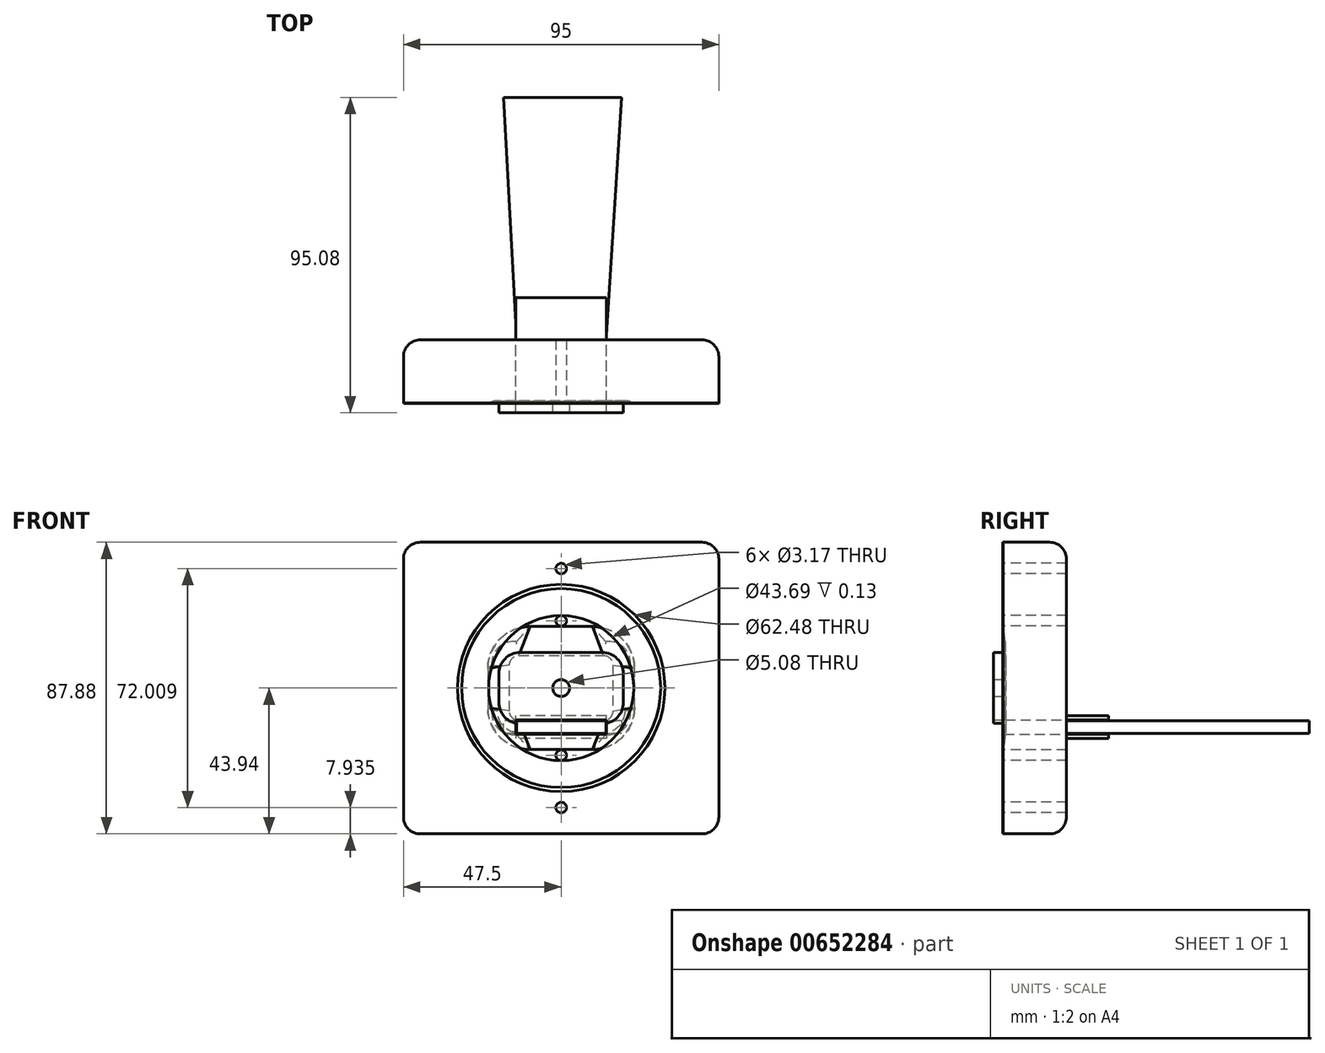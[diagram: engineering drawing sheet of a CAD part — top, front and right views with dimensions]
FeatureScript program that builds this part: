
annotation { "Feature Type Name" : "Feature", "Feature Type Description" : "" }
export const myFeature = defineFeature(function(context is Context, id is Id, definition is map)
    precondition{}
    {
        {
            assignVariable(context, id + "F0", {"name" : "RingLightT", "anyValue" : .13});
        }
        {
            assignVariable(context, id + "F1", {"name" : "CamDepth", "anyValue" : .688});
        }
        {
            var Q0;
            Q0=qCreatedBy(makeId("Front.planeOp"),FACE);
            var sketch = newSketch(context, id + "F2", { "sketchPlane" : qUnion([Q0])});
            skCircle(sketch, "E0", {"center": v(0, 0) * mm, "radius": 21.84 * mm});
            skCircle(sketch, "E1", {"center": v(0, 0) * mm, "radius": 29.97 * mm});
            skSolve(sketch);
        }
        {
            var Q0;
            Q0=qSketchRegion(id+"F2",true);
            extrude(context, id + "F3", {"entities" : qUnion([Q0]), "depth" : (getVariable(context, 'RingLightT')) * mm, "offsetDistance" : 25.4 * mm});
        }
        {
            var Q0;
            Q0=qCreatedBy(makeId("Front.planeOp"),FACE);
            var sketch = newSketch(context, id + "F4", { "sketchPlane" : qUnion([Q0])});
            skLineSegment(sketch, "E2.bottom", {"start": v(12.38, 10.73) * mm, "end": v(-12.38, 10.73) * mm});
            skLineSegment(sketch, "E2.top", {"start": v(12.38, -10.73) * mm, "end": v(-12.38, -10.73) * mm});
            skLineSegment(sketch, "E2.left", {"start": v(18.73, 4.38) * mm, "end": v(18.73, -4.38) * mm});
            skLineSegment(sketch, "E2.right", {"start": v(-18.73, 4.38) * mm, "end": v(-18.73, -4.38) * mm});
            skPoint(sketch, "E2.middle", {"position": v(0, 0) * mm});
            skPoint(sketch, "E3.visualSharp", {"position": v(-18.73, 10.73) * mm});
            skArc(sketch, "E3.filletArc", {"start": v(-12.38, 10.73) * mm, "mid": v(-16.87, 8.87) * mm, "end": v(-18.73, 4.38) * mm});
            skPoint(sketch, "E4.visualSharp", {"position": v(18.73, 10.73) * mm});
            skArc(sketch, "E4.filletArc", {"start": v(18.73, 4.38) * mm, "mid": v(16.87, 8.87) * mm, "end": v(12.38, 10.73) * mm});
            skPoint(sketch, "E5.visualSharp", {"position": v(18.73, -10.73) * mm});
            skArc(sketch, "E5.filletArc", {"start": v(12.38, -10.73) * mm, "mid": v(16.87, -8.87) * mm, "end": v(18.73, -4.38) * mm});
            skPoint(sketch, "E6.visualSharp", {"position": v(-18.73, -10.73) * mm});
            skArc(sketch, "E6.filletArc", {"start": v(-18.73, -4.38) * mm, "mid": v(-16.87, -8.87) * mm, "end": v(-12.38, -10.73) * mm});
            skCircle(sketch, "E7", {"center": v(0, 0) * mm, "radius": 2.54 * mm});
            skSolve(sketch);
        }
        {
            var Q0;
            Q0=qSketchRegion(id+"F4",true);
            extrude(context, id + "F5", {"entities" : qUnion([Q0]), "depth" : 2.95 * mm, "offsetDistance" : 25.4 * mm});
        }
        {
            var Q0;
            Q0=qCreatedBy(makeId("Front.planeOp"),FACE);
            cPlane(context, id + "F6", {"entities" : qUnion([Q0]), "cplaneType" : CPlaneType.OFFSET, "offset" : (getVariable(context, 'CamDepth')) * mm, "oppositeDirection" : true, "width" : 152.4 * mm, "height" : 152.4 * mm});
        }
        {
            var Q0;
            Q0=qCreatedBy(id+"F6.planeOp",FACE);
            var sketch = newSketch(context, id + "F7", { "sketchPlane" : qUnion([Q0])});
            skLineSegment(sketch, "E8.bottom", {"start": v(13.7, 13.68) * mm, "end": v(-13.7, 13.68) * mm});
            skLineSegment(sketch, "E8.top", {"start": v(13.7, -13.68) * mm, "end": v(-13.7, -13.68) * mm});
            skLineSegment(sketch, "E8.left", {"start": v(20.04, 7.33) * mm, "end": v(20.04, -7.33) * mm});
            skLineSegment(sketch, "E8.right", {"start": v(-20.04, 7.33) * mm, "end": v(-20.04, -7.33) * mm});
            skPoint(sketch, "E8.middle", {"position": v(0, 0) * mm});
            skPoint(sketch, "E9.visualSharp", {"position": v(-20.04, 13.68) * mm});
            skArc(sketch, "E9.filletArc", {"start": v(-13.7, 13.68) * mm, "mid": v(-18.18, 11.82) * mm, "end": v(-20.04, 7.33) * mm});
            skPoint(sketch, "E10.visualSharp", {"position": v(20.04, 13.68) * mm});
            skArc(sketch, "E10.filletArc", {"start": v(20.04, 7.33) * mm, "mid": v(18.18, 11.82) * mm, "end": v(13.7, 13.68) * mm});
            skPoint(sketch, "E11.visualSharp", {"position": v(20.04, -13.68) * mm});
            skArc(sketch, "E11.filletArc", {"start": v(13.7, -13.68) * mm, "mid": v(18.18, -11.82) * mm, "end": v(20.04, -7.33) * mm});
            skPoint(sketch, "E12.visualSharp", {"position": v(-20.04, -13.68) * mm});
            skArc(sketch, "E12.filletArc", {"start": v(-20.04, -7.33) * mm, "mid": v(-18.18, -11.82) * mm, "end": v(-13.7, -13.68) * mm});
            skSolve(sketch);
        }
        {
            var Q0;
            Q0=qCreatedBy(makeId("Front.planeOp"),FACE);
            var sketch = newSketch(context, id + "F8", { "sketchPlane" : qUnion([Q0])});
            skLineSegment(sketch, "E13.bottom", {"start": v(9.4, 18.54) * mm, "end": v(-9.4, 18.54) * mm});
            skLineSegment(sketch, "E13.top", {"start": v(9.4, -18.54) * mm, "end": v(-9.4, -18.54) * mm});
            skLineSegment(sketch, "E13.left", {"start": v(22.1, 5.84) * mm, "end": v(22.1, -5.84) * mm});
            skLineSegment(sketch, "E13.right", {"start": v(-22.1, 5.84) * mm, "end": v(-22.1, -5.84) * mm});
            skPoint(sketch, "E13.middle", {"position": v(0, 0) * mm});
            skPoint(sketch, "E14.visualSharp", {"position": v(-22.1, 18.54) * mm});
            skArc(sketch, "E14.filletArc", {"start": v(-9.4, 18.54) * mm, "mid": v(-18.38, 14.82) * mm, "end": v(-22.1, 5.84) * mm});
            skPoint(sketch, "E15.visualSharp", {"position": v(22.1, 18.54) * mm});
            skArc(sketch, "E15.filletArc", {"start": v(22.1, 5.84) * mm, "mid": v(18.38, 14.82) * mm, "end": v(9.4, 18.54) * mm});
            skPoint(sketch, "E16.visualSharp", {"position": v(22.1, -18.54) * mm});
            skArc(sketch, "E16.filletArc", {"start": v(9.4, -18.54) * mm, "mid": v(18.38, -14.82) * mm, "end": v(22.1, -5.84) * mm});
            skPoint(sketch, "E17.visualSharp", {"position": v(-22.1, -18.54) * mm});
            skArc(sketch, "E17.filletArc", {"start": v(-22.1, -5.84) * mm, "mid": v(-18.38, -14.82) * mm, "end": v(-9.4, -18.54) * mm});
            skSolve(sketch);
        }
        {
            var Q1;
            Q1=makeQuery(id+"F7.imprint","IMPRINT",FACE,{"disambiguationData":[TD([[makeQuery(id+"F7.imprint","IMPRINT",EDGE,{"derivedFrom":sQuery(id+"F7.wireOp",EDGE,"E8.bottom")}),1.0]])]});
            var Q2;
            Q2=makeQuery(id+"F8.imprint","IMPRINT",FACE,{"disambiguationData":[TD([[makeQuery(id+"F8.imprint","IMPRINT",EDGE,{"derivedFrom":sQuery(id+"F8.wireOp",EDGE,"E13.bottom")}),1.0]])]});
            loft(context, id + "F9", {"operationType" : NewBodyOperationType.ADD, "sheetProfilesArray" : [{ "sheetProfileEntities" : qUnion([Q1]) }, { "sheetProfileEntities" : qUnion([Q2]) }]});
        }
        {
            var Q0;
            Q0=makeQuery(id+"F9.opLoft","CAP_FACE",FACE,{"disambiguationData":[OSD([makeQuery(id+"F7.imprint","IMPRINT",FACE,{"disambiguationData":[TD([[makeQuery(id+"F7.imprint","IMPRINT",EDGE,{"derivedFrom":sQuery(id+"F7.wireOp",EDGE,"E8.bottom")}),1.0]])]})])],"isStart":true});
            var sketch = newSketch(context, id + "F10", { "sketchPlane" : qUnion([Q0])});
            skLineSegment(sketch, "E18.bottom", {"start": v(-12.38, -13.68) * mm, "end": v(12.38, -13.68) * mm});
            skLineSegment(sketch, "E18.top", {"start": v(-12.38, -9.84) * mm, "end": v(12.38, -9.84) * mm});
            skLineSegment(sketch, "E18.left", {"start": v(-12.38, -13.68) * mm, "end": v(-12.38, -9.84) * mm});
            skLineSegment(sketch, "E18.right", {"start": v(12.38, -13.68) * mm, "end": v(12.38, -9.84) * mm});
            skPoint(sketch, "E19", {"position": v(0, -13.68) * mm});
            skSolve(sketch);
        }
        {
            var Q0;
            Q0=makeQuery(id+"F9.opLoft","CAP_FACE",FACE,{"disambiguationData":[OSD([makeQuery(id+"F7.imprint","IMPRINT",FACE,{"disambiguationData":[TD([[makeQuery(id+"F7.imprint","IMPRINT",EDGE,{"derivedFrom":sQuery(id+"F7.wireOp",EDGE,"E8.bottom")}),1.0]])]})])],"isStart":true});
            cPlane(context, id + "F11", {"entities" : qUnion([Q0]), "cplaneType" : CPlaneType.OFFSET, "offset" : 91.44 * mm, "width" : 152.4 * mm, "height" : 152.4 * mm});
        }
        {
            var Q0;
            Q0=qCreatedBy(id+"F11.planeOp",FACE);
            var sketch = newSketch(context, id + "F12", { "sketchPlane" : qUnion([Q0])});
            skLineSegment(sketch, "E20.0", {"start": v(-12.38, -9.84) * mm, "end": v(12.38, -9.84) * mm, "construction": true});
            skLineSegment(sketch, "E21.0", {"start": v(12.38, -13.68) * mm, "end": v(12.38, -9.84) * mm, "construction": true});
            skLineSegment(sketch, "E22.0", {"start": v(-12.38, -13.68) * mm, "end": v(-12.38, -9.84) * mm, "construction": true});
            skLineSegment(sketch, "E23.0", {"start": v(-12.38, -13.68) * mm, "end": v(12.38, -13.68) * mm, "construction": true});
            skLineSegment(sketch, "E24", {"start": v(-18.23, -9.84) * mm, "end": v(17.33, -9.84) * mm});
            skLineSegment(sketch, "E25", {"start": v(-18.23, -9.84) * mm, "end": v(-18.23, -13.68) * mm});
            skLineSegment(sketch, "E26", {"start": v(-18.23, -13.68) * mm, "end": v(17.33, -13.68) * mm});
            skLineSegment(sketch, "E27", {"start": v(17.33, -13.68) * mm, "end": v(17.33, -9.84) * mm});
            skSolve(sketch);
        }
        {
            var Q0;
            Q0=qSketchRegion(id+"F10",true);
            var Q1;
            Q1=qSketchRegion(id+"F12",true);
            loft(context, id + "F13", {"sheetProfilesArray" : [{ "sheetProfileEntities" : qUnion([Q0]) }, { "sheetProfileEntities" : qUnion([Q1]) }]});
        }
        {
            var Q0;
            Q0=makeQuery(id+"F9.opLoft","MID_CAP_EDGE",EDGE,{"disambiguationData":[OSD([sQuery(id+"F7.wireOp",EDGE,"E8.bottom"),sQuery(id+"F7.wireOp",EDGE,"E9.filletArc"),sQuery(id+"F7.wireOp",EDGE,"E10.filletArc")])],"capPos":0.0});
            fillet(context, id + "F14", {"entities" : qUnion([Q0]), "radius" : 5.08 * mm, "tangentPropagation" : true, "allowEdgeOverflow" : false});
        }
        {
            var Q0;
            {var subQ2=sQuery(id+"F8.wireOp",EDGE,"E13.bottom");Q0=makeQuery(id+"F9.boolean.opBoolean","SPLIT",FACE,{"disambiguationData":[TD([makeQuery(id+"F5.opExtrude","SWEPT_FACE",FACE,{"disambiguationData":[OSD([sQuery(id+"F4.wireOp",EDGE,"E2.bottom")])]})])],"derivedFrom":makeQuery(id+"F9.opLoft","CAP_FACE",FACE,{"disambiguationData":[OSD([makeQuery(id+"F8.imprint","IMPRINT",FACE,{"disambiguationData":[TD([[makeQuery(id+"F8.imprint","IMPRINT",EDGE,{"derivedFrom":subQ2}),1.0]])]})])],"isStart":true})});}
            var sketch = newSketch(context, id + "F15", { "sketchPlane" : qUnion([Q0])});
            skLineSegment(sketch, "E28.bottom", {"start": v(47.5, 43.94) * mm, "end": v(-47.5, 43.94) * mm});
            skLineSegment(sketch, "E28.top", {"start": v(47.5, -43.94) * mm, "end": v(-47.5, -43.94) * mm});
            skLineSegment(sketch, "E28.left", {"start": v(47.5, 43.94) * mm, "end": v(47.5, -43.94) * mm});
            skLineSegment(sketch, "E28.right", {"start": v(-47.5, 43.94) * mm, "end": v(-47.5, -43.94) * mm});
            skPoint(sketch, "E28.middle", {"position": v(0, 0) * mm});
            skCircle(sketch, "E29", {"center": v(0, 0) * mm, "radius": 31.24 * mm});
            skSolve(sketch);
        }
        {
            var Q0;
            Q0=qSketchRegion(id+"F15",true);
            extrude(context, id + "F16", {"entities" : qUnion([Q0]), "depth" : (getVariable(context, 'RingLightT')) * mm, "offsetDistance" : 25.4 * mm});
        }
        {
            var Q0;
            Q0=makeQuery(id+"F16.opExtrude","CAP_FACE",FACE,{"disambiguationData":[OSD([sQuery(id+"F15.wireOp",EDGE,"E28.bottom"),sQuery(id+"F15.wireOp",EDGE,"E28.top"),sQuery(id+"F15.wireOp",EDGE,"E28.left"),sQuery(id+"F15.wireOp",EDGE,"E28.right"),sQuery(id+"F15.wireOp",EDGE,"E29")])],"isStart":true});
            var sketch = newSketch(context, id + "F17", { "sketchPlane" : qUnion([Q0])});
            skLineSegment(sketch, "E30.bottom", {"start": v(47.5, 43.94) * mm, "end": v(-47.5, 43.94) * mm});
            skLineSegment(sketch, "E30.top", {"start": v(47.5, -43.94) * mm, "end": v(-47.5, -43.94) * mm});
            skLineSegment(sketch, "E30.left", {"start": v(47.5, 43.94) * mm, "end": v(47.5, -43.94) * mm});
            skLineSegment(sketch, "E30.right", {"start": v(-47.5, 43.94) * mm, "end": v(-47.5, -43.94) * mm});
            skPoint(sketch, "E30.middle", {"position": v(0, 0) * mm});
            skSolve(sketch);
        }
        {
            var Q0;
            Q0=qSketchRegion(id+"F17",true);
            extrude(context, id + "F18", {"entities" : qUnion([Q0]), "depth" : 19.05 * mm, "offsetDistance" : 25.4 * mm});
        }
        {
            var Q0;
            Q0=qCreatedBy(makeId("Front.planeOp"),FACE);
            var sketch = newSketch(context, id + "F19", { "sketchPlane" : qUnion([Q0])});
            skFitSpline(sketch, "E31.0", {"points": [v(-22.1, 5.84) * mm, v(-22.1, 6.26) * mm, v(-22.06, 7.09) * mm, v(-21.87, 8.32) * mm, v(-21.57, 9.53) * mm, v(-21.15, 10.71) * mm, v(-20.62, 11.84) * mm, v(-19.97, 12.9) * mm, v(-19.23, 13.91) * mm, v(-18.4, 14.84) * mm, v(-17.47, 15.67) * mm, v(-16.46, 16.42) * mm, v(-15.4, 17.06) * mm, v(-14.27, 17.6) * mm, v(-13.1, 18.01) * mm, v(-11.88, 18.32) * mm, v(-10.64, 18.5) * mm, v(-9.82, 18.54) * mm, v(-9.4, 18.54) * mm]});
            skLineSegment(sketch, "E32.0", {"start": v(9.4, 18.54) * mm, "end": v(-9.4, 18.54) * mm});
            skFitSpline(sketch, "E33.0", {"points": [v(9.4, 18.54) * mm, v(9.81, 18.54) * mm, v(10.64, 18.5) * mm, v(11.88, 18.32) * mm, v(13.1, 18.02) * mm, v(14.27, 17.6) * mm, v(15.4, 17.06) * mm, v(16.47, 16.42) * mm, v(17.47, 15.68) * mm, v(18.4, 14.84) * mm, v(19.23, 13.91) * mm, v(19.97, 12.9) * mm, v(20.62, 11.84) * mm, v(21.15, 10.7) * mm, v(21.57, 9.54) * mm, v(21.87, 8.32) * mm, v(22.06, 7.09) * mm, v(22.1, 6.26) * mm, v(22.1, 5.84) * mm]});
            skLineSegment(sketch, "E34.0", {"start": v(-22.1, 5.84) * mm, "end": v(-22.1, -5.84) * mm});
            skFitSpline(sketch, "E35.0", {"points": [v(22.1, -5.84) * mm, v(22.1, -6.26) * mm, v(22.06, -7.09) * mm, v(21.87, -8.32) * mm, v(21.57, -9.53) * mm, v(21.15, -10.71) * mm, v(20.62, -11.84) * mm, v(19.97, -12.9) * mm, v(19.23, -13.91) * mm, v(18.4, -14.84) * mm, v(17.47, -15.67) * mm, v(16.46, -16.42) * mm, v(15.4, -17.06) * mm, v(14.27, -17.6) * mm, v(13.1, -18.01) * mm, v(11.88, -18.32) * mm, v(10.64, -18.5) * mm, v(9.82, -18.54) * mm, v(9.4, -18.54) * mm]});
            skLineSegment(sketch, "E36.0", {"start": v(-9.4, -18.54) * mm, "end": v(9.4, -18.54) * mm});
            skFitSpline(sketch, "E37.0", {"points": [v(-9.4, -18.54) * mm, v(-9.81, -18.54) * mm, v(-10.64, -18.5) * mm, v(-11.88, -18.32) * mm, v(-13.1, -18.02) * mm, v(-14.27, -17.6) * mm, v(-15.4, -17.06) * mm, v(-16.47, -16.42) * mm, v(-17.47, -15.68) * mm, v(-18.4, -14.84) * mm, v(-19.23, -13.91) * mm, v(-19.97, -12.9) * mm, v(-20.62, -11.84) * mm, v(-21.15, -10.7) * mm, v(-21.57, -9.54) * mm, v(-21.87, -8.32) * mm, v(-22.06, -7.09) * mm, v(-22.1, -6.26) * mm, v(-22.1, -5.84) * mm]});
            skLineSegment(sketch, "E38.0", {"start": v(22.1, -5.84) * mm, "end": v(22.1, 5.84) * mm});
            skSolve(sketch);
        }
        {
            var Q0;
            Q0=makeQuery(id+"F9.opLoft","CAP_FACE",FACE,{"disambiguationData":[OSD([makeQuery(id+"F7.imprint","IMPRINT",FACE,{"disambiguationData":[TD([[makeQuery(id+"F7.imprint","IMPRINT",EDGE,{"derivedFrom":sQuery(id+"F7.wireOp",EDGE,"E8.bottom")}),1.0]])]})])],"isStart":true});
            var sketch = newSketch(context, id + "F20", { "sketchPlane" : qUnion([Q0])});
            skFitSpline(sketch, "E39.0", {"points": [v(-12.78, 9.82) * mm, v(-12.96, 9.82) * mm, v(-13.32, 9.77) * mm, v(-13.85, 9.6) * mm, v(-14.25, 9.37) * mm, v(-14.54, 9.14) * mm, v(-14.74, 8.95) * mm, v(-14.91, 8.74) * mm, v(-15.07, 8.52) * mm, v(-15.2, 8.27) * mm, v(-15.35, 7.94) * mm, v(-15.48, 7.5) * mm, v(-15.52, 7.13) * mm, v(-15.52, 6.95) * mm]});
            skLineSegment(sketch, "E40.0", {"start": v(12.78, 9.82) * mm, "end": v(-12.78, 9.82) * mm});
            skFitSpline(sketch, "E41.0", {"points": [v(15.52, 6.95) * mm, v(15.52, 7.13) * mm, v(15.49, 7.5) * mm, v(15.33, 8.03) * mm, v(15.09, 8.52) * mm, v(14.75, 8.96) * mm, v(14.34, 9.32) * mm, v(13.85, 9.6) * mm, v(13.33, 9.77) * mm, v(12.96, 9.82) * mm, v(12.78, 9.82) * mm]});
            skLineSegment(sketch, "E42.0", {"start": v(15.52, -6.95) * mm, "end": v(15.52, 6.95) * mm});
            skFitSpline(sketch, "E43.0", {"points": [v(12.78, -9.82) * mm, v(12.96, -9.82) * mm, v(13.32, -9.77) * mm, v(13.85, -9.6) * mm, v(14.25, -9.37) * mm, v(14.54, -9.14) * mm, v(14.74, -8.95) * mm, v(14.91, -8.74) * mm, v(15.07, -8.52) * mm, v(15.2, -8.27) * mm, v(15.35, -7.94) * mm, v(15.48, -7.5) * mm, v(15.52, -7.13) * mm, v(15.52, -6.95) * mm]});
            skLineSegment(sketch, "E44.0", {"start": v(-12.78, -9.82) * mm, "end": v(12.78, -9.82) * mm});
            skFitSpline(sketch, "E45.0", {"points": [v(-15.52, -6.95) * mm, v(-15.52, -7.13) * mm, v(-15.49, -7.5) * mm, v(-15.33, -8.03) * mm, v(-15.09, -8.52) * mm, v(-14.75, -8.96) * mm, v(-14.34, -9.32) * mm, v(-13.85, -9.6) * mm, v(-13.33, -9.77) * mm, v(-12.96, -9.82) * mm, v(-12.78, -9.82) * mm]});
            skLineSegment(sketch, "E46.0", {"start": v(-15.52, 6.95) * mm, "end": v(-15.52, -6.95) * mm});
            skSolve(sketch);
        }
        {
            var Q1;
            Q1=qSketchRegion(id+"F20",true);
            var Q2;
            Q2=qSketchRegion(id+"F19",true);
            loft(context, id + "F21", {"operationType" : NewBodyOperationType.REMOVE, "sheetProfilesArray" : [{ "sheetProfileEntities" : qUnion([Q1]) }, { "sheetProfileEntities" : qUnion([Q2]) }]});
        }
        {
            var Q0;
            Q0=makeQuery(id+"F18.opExtrude","CAP_FACE",FACE,{"disambiguationData":[OSD([sQuery(id+"F17.wireOp",EDGE,"E30.bottom"),sQuery(id+"F17.wireOp",EDGE,"E30.top"),sQuery(id+"F17.wireOp",EDGE,"E30.left"),sQuery(id+"F17.wireOp",EDGE,"E30.right")])],"isStart":false});
            var sketch = newSketch(context, id + "F22", { "sketchPlane" : qUnion([Q0])});
            skLineSegment(sketch, "E47.0", {"start": v(-13.65, -9.59) * mm, "end": v(13.65, -9.59) * mm});
            skLineSegment(sketch, "E47.1", {"start": v(-13.65, -13.93) * mm, "end": v(-13.65, -9.59) * mm});
            skLineSegment(sketch, "E47.2", {"start": v(13.65, -13.93) * mm, "end": v(-13.65, -13.93) * mm});
            skLineSegment(sketch, "E47.3", {"start": v(13.65, -13.93) * mm, "end": v(13.65, -9.59) * mm});
            skLineSegment(sketch, "E48.0", {"start": v(-12.38, -9.84) * mm, "end": v(12.38, -9.84) * mm, "construction": true});
            skLineSegment(sketch, "E49.0", {"start": v(-12.38, -13.68) * mm, "end": v(-12.38, -9.84) * mm, "construction": true});
            skLineSegment(sketch, "E50.0", {"start": v(-12.38, -13.68) * mm, "end": v(12.38, -13.68) * mm, "construction": true});
            skPoint(sketch, "E51.0", {"position": v(12.38, -11.76) * mm});
            skLineSegment(sketch, "E52.0", {"start": v(12.38, -13.68) * mm, "end": v(12.38, -9.84) * mm, "construction": true});
            skSolve(sketch);
        }
        {
            var Q0;
            Q0=qSketchRegion(id+"F22",true);
            extrude(context, id + "F23", {"entities" : qUnion([Q0]), "operationType" : NewBodyOperationType.REMOVE, "oppositeDirection" : true, "depth" : 25.4 * mm, "offsetDistance" : 25.4 * mm});
        }
        {
            var Q0;
            Q0=makeQuery(id+"F18.opExtrude","CAP_FACE",FACE,{"disambiguationData":[OSD([sQuery(id+"F17.wireOp",EDGE,"E30.bottom"),sQuery(id+"F17.wireOp",EDGE,"E30.top"),sQuery(id+"F17.wireOp",EDGE,"E30.left"),sQuery(id+"F17.wireOp",EDGE,"E30.right")])],"isStart":true});
            var sketch = newSketch(context, id + "F24", { "sketchPlane" : qUnion([Q0])});
            skCircle(sketch, "E53", {"center": v(0, 20.26) * mm, "radius": 1.59 * mm});
            skCircle(sketch, "E54", {"center": v(0, -20.26) * mm, "radius": 1.59 * mm});
            skSolve(sketch);
        }
        {
            var Q0;
            Q0=qSketchRegion(id+"F24",true);
            var Q1;
            Q1=makeQuery(id+"F18.opExtrude","CAP_FACE",FACE,{"disambiguationData":[OSD([sQuery(id+"F17.wireOp",EDGE,"E30.bottom"),sQuery(id+"F17.wireOp",EDGE,"E30.top"),sQuery(id+"F17.wireOp",EDGE,"E30.left"),sQuery(id+"F17.wireOp",EDGE,"E30.right")])],"isStart":false});
            extrude(context, id + "F25", {"entities" : qUnion([Q0]), "operationType" : NewBodyOperationType.REMOVE, "endBound" : BoundingType.UP_TO_SURFACE, "oppositeDirection" : true, "depth" : 25.4 * mm, "endBoundEntityFace" : qUnion([Q1]), "offsetDistance" : 25.4 * mm});
        }
        {
            var Q0;
            Q0=makeQuery(id+"F16.opExtrude","CAP_FACE",FACE,{"disambiguationData":[OSD([sQuery(id+"F15.wireOp",EDGE,"E28.bottom"),sQuery(id+"F15.wireOp",EDGE,"E28.top"),sQuery(id+"F15.wireOp",EDGE,"E28.left"),sQuery(id+"F15.wireOp",EDGE,"E28.right"),sQuery(id+"F15.wireOp",EDGE,"E29")])],"isStart":false});
            var sketch = newSketch(context, id + "F26", { "sketchPlane" : qUnion([Q0])});
            skCircle(sketch, "E55", {"center": v(0, 36) * mm, "radius": 1.59 * mm});
            skCircle(sketch, "E56", {"center": v(0, -36) * mm, "radius": 1.59 * mm});
            skSolve(sketch);
        }
        {
            var Q0;
            Q0=qSketchRegion(id+"F26",true);
            var Q1;
            Q1=makeQuery(id+"F18.opExtrude","CAP_FACE",FACE,{"disambiguationData":[OSD([sQuery(id+"F17.wireOp",EDGE,"E30.bottom"),sQuery(id+"F17.wireOp",EDGE,"E30.top"),sQuery(id+"F17.wireOp",EDGE,"E30.left"),sQuery(id+"F17.wireOp",EDGE,"E30.right")])],"isStart":false});
            extrude(context, id + "F27", {"entities" : qUnion([Q0]), "operationType" : NewBodyOperationType.REMOVE, "endBound" : BoundingType.UP_TO_SURFACE, "oppositeDirection" : true, "depth" : 25.4 * mm, "endBoundEntityFace" : qUnion([Q1]), "offsetDistance" : 25.4 * mm});
        }
        {
            var Q0;
            Q0=makeQuery(id+"F18.opExtrude","CAP_FACE",FACE,{"disambiguationData":[OSD([sQuery(id+"F17.wireOp",EDGE,"E30.bottom"),sQuery(id+"F17.wireOp",EDGE,"E30.top"),sQuery(id+"F17.wireOp",EDGE,"E30.left"),sQuery(id+"F17.wireOp",EDGE,"E30.right")])],"isStart":false});
            var sketch = newSketch(context, id + "F28", { "sketchPlane" : qUnion([Q0])});
            skLineSegment(sketch, "E57.bottom", {"start": v(-13.65, -9.59) * mm, "end": v(13.65, -9.59) * mm});
            skLineSegment(sketch, "E57.top", {"start": v(-13.65, -8.32) * mm, "end": v(13.65, -8.32) * mm});
            skLineSegment(sketch, "E57.left", {"start": v(-13.65, -9.59) * mm, "end": v(-13.65, -8.32) * mm});
            skLineSegment(sketch, "E57.right", {"start": v(13.65, -9.59) * mm, "end": v(13.65, -8.32) * mm});
            skLineSegment(sketch, "E58.bottom", {"start": v(-13.65, -13.93) * mm, "end": v(13.65, -13.93) * mm});
            skLineSegment(sketch, "E58.top", {"start": v(-13.65, -15.2) * mm, "end": v(13.65, -15.2) * mm});
            skLineSegment(sketch, "E58.left", {"start": v(-13.65, -13.93) * mm, "end": v(-13.65, -15.2) * mm});
            skLineSegment(sketch, "E58.right", {"start": v(13.65, -13.93) * mm, "end": v(13.65, -15.2) * mm});
            skSolve(sketch);
        }
        {
            var Q0;
            Q0=qSketchRegion(id+"F28",true);
            extrude(context, id + "F29", {"entities" : qUnion([Q0]), "operationType" : NewBodyOperationType.ADD, "depth" : 12.7 * mm, "offsetDistance" : 25.4 * mm});
        }
        {
            var Q0;
            Q0=makeQuery(id+"F18.opExtrude","SWEPT_EDGE",EDGE,{"disambiguationData":[OSD([sQuery(id+"F17.wireOp",EDGE,"E30.top"),sQuery(id+"F17.wireOp",EDGE,"E30.left")])]});
            var Q1;
            Q1=makeQuery(id+"F16.opExtrude","SWEPT_EDGE",EDGE,{"disambiguationData":[OSD([sQuery(id+"F15.wireOp",EDGE,"E28.top"),sQuery(id+"F15.wireOp",EDGE,"E28.right")])]});
            var Q2;
            Q2=makeQuery(id+"F18.opExtrude","CAP_EDGE",EDGE,{"disambiguationData":[OSD([sQuery(id+"F17.wireOp",EDGE,"E30.top")])],"isStart":false});
            var Q3;
            Q3=makeQuery(id+"F18.opExtrude","SWEPT_EDGE",EDGE,{"disambiguationData":[OSD([sQuery(id+"F17.wireOp",EDGE,"E30.top"),sQuery(id+"F17.wireOp",EDGE,"E30.right")])]});
            var Q4;
            Q4=makeQuery(id+"F16.opExtrude","SWEPT_EDGE",EDGE,{"disambiguationData":[OSD([sQuery(id+"F15.wireOp",EDGE,"E28.top"),sQuery(id+"F15.wireOp",EDGE,"E28.left")])]});
            var Q5;
            Q5=makeQuery(id+"F18.opExtrude","CAP_EDGE",EDGE,{"disambiguationData":[OSD([sQuery(id+"F17.wireOp",EDGE,"E30.right")])],"isStart":false});
            var Q6;
            Q6=makeQuery(id+"F18.opExtrude","SWEPT_EDGE",EDGE,{"disambiguationData":[OSD([sQuery(id+"F17.wireOp",EDGE,"E30.bottom"),sQuery(id+"F17.wireOp",EDGE,"E30.right")])]});
            var Q7;
            Q7=makeQuery(id+"F16.opExtrude","SWEPT_EDGE",EDGE,{"disambiguationData":[OSD([sQuery(id+"F15.wireOp",EDGE,"E28.bottom"),sQuery(id+"F15.wireOp",EDGE,"E28.left")])]});
            var Q8;
            Q8=makeQuery(id+"F18.opExtrude","CAP_EDGE",EDGE,{"disambiguationData":[OSD([sQuery(id+"F17.wireOp",EDGE,"E30.bottom")])],"isStart":false});
            var Q9;
            Q9=makeQuery(id+"F18.opExtrude","SWEPT_EDGE",EDGE,{"disambiguationData":[OSD([sQuery(id+"F17.wireOp",EDGE,"E30.bottom"),sQuery(id+"F17.wireOp",EDGE,"E30.left")])]});
            var Q10;
            Q10=makeQuery(id+"F16.opExtrude","SWEPT_EDGE",EDGE,{"disambiguationData":[OSD([sQuery(id+"F15.wireOp",EDGE,"E28.bottom"),sQuery(id+"F15.wireOp",EDGE,"E28.right")])]});
            var Q11;
            Q11=makeQuery(id+"F18.opExtrude","CAP_EDGE",EDGE,{"disambiguationData":[OSD([sQuery(id+"F17.wireOp",EDGE,"E30.left")])],"isStart":false});
            fillet(context, id + "F30", {"entities" : qUnion([Q0, Q1, Q2, Q3, Q4, Q5, Q6, Q7, Q8, Q9, Q10, Q11]), "radius" : 5.08 * mm, "tangentPropagation" : true, "allowEdgeOverflow" : false});
        }
    });
